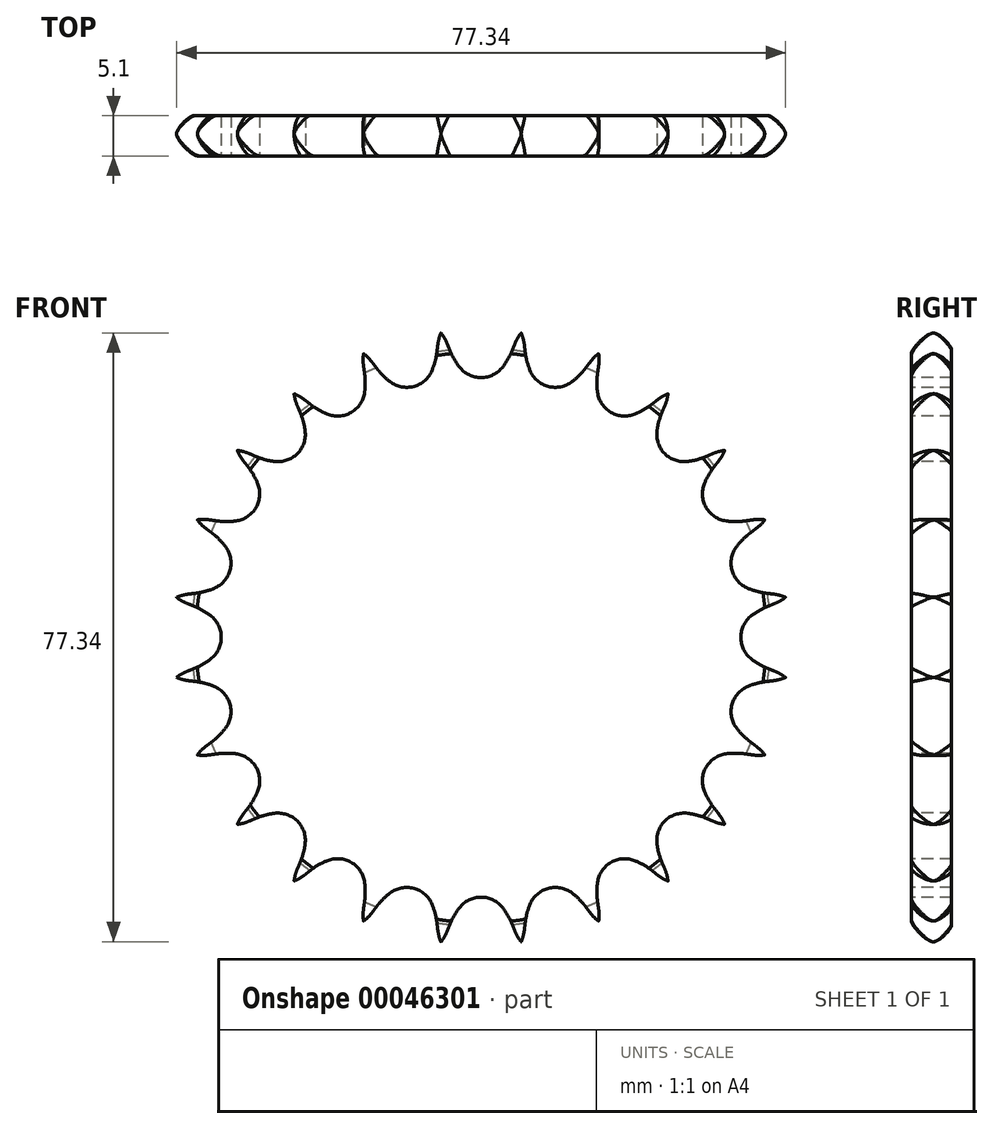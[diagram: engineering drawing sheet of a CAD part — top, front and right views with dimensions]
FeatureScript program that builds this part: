
annotation { "Feature Type Name" : "Feature", "Feature Type Description" : "" }
export const myFeature = defineFeature(function(context is Context, id is Id, definition is map)
    precondition{}
    {
        {
            var Q0;
            Q0=qCreatedBy(makeId("Right.planeOp"),FACE);
            var sketch = newSketch(context, id + "F0", { "sketchPlane" : qUnion([Q0])});
            skLineSegment(sketch, "E0", {"start": v(0, 0) * mm, "end": v(5.1, 0) * mm, "construction": true});
            skLineSegment(sketch, "E1", {"start": v(0, 39) * mm, "end": v(5.1, 39) * mm});
            skLineSegment(sketch, "E2", {"start": v(5.1, 39) * mm, "end": v(5.1, 30) * mm});
            skLineSegment(sketch, "E3", {"start": v(5.1, 30) * mm, "end": v(5.1, 30) * mm});
            skLineSegment(sketch, "E4", {"start": v(5.1, 30) * mm, "end": v(5.1, 0) * mm});
            skLineSegment(sketch, "E5", {"start": v(0, 0) * mm, "end": v(0, 39) * mm});
            skLineSegment(sketch, "E6.0.MirrorCS", {"start": v(0, -39) * mm, "end": v(5.1, -39) * mm});
            skLineSegment(sketch, "E6.1.MirrorCS", {"start": v(5.1, -39) * mm, "end": v(5.1, -30) * mm});
            skLineSegment(sketch, "E6.3.MirrorCS", {"start": v(5.1, -30) * mm, "end": v(5.1, 0) * mm});
            skLineSegment(sketch, "E6.4.MirrorCS", {"start": v(5.1, -30) * mm, "end": v(5.1, -30) * mm});
            skLineSegment(sketch, "E6.5.MirrorCS", {"start": v(0, 0) * mm, "end": v(0, -39) * mm});
            skLineSegment(sketch, "E7", {"start": v(0, 0) * mm, "end": v(5.1, 0) * mm});
            skLineSegment(sketch, "E8", {"start": v(5.1, 30) * mm, "end": v(0, 30) * mm, "construction": true});
            skLineSegment(sketch, "E9", {"start": v(5.1, -30) * mm, "end": v(0, -30) * mm, "construction": true});
            skSolve(sketch);
        }
        {
            var Q0;
            Q0=makeQuery(id+"F0.imprint","IMPRINT",FACE,{"disambiguationData":[TD([[makeQuery(id+"F0.imprint","IMPRINT",EDGE,{"derivedFrom":sQuery(id+"F0.wireOp",EDGE,"E1")}),-1.0]])]});
            var Q1;
            Q1=sQuery(id+"F0.wireOp",EDGE,"E0");
            revolve(context, id + "F1", {"entities" : qUnion([Q0]), "axis" : qUnion([Q1]), "revolveType" : RevolveType.FULL});
        }
        {
            var Q0;
            Q0=makeQuery(id+"F1.opRevolve","SWEPT_EDGE",EDGE,{"disambiguationData":[OSD([sQuery(id+"F0.wireOp",EDGE,"E1"),sQuery(id+"F0.wireOp",EDGE,"E5")])]});
            fillet(context, id + "F2", {"entities" : qUnion([Q0]), "radius" : 2.75 * mm, "tangentPropagation" : true, "rho" : 0.2, "crossSection" : FilletCrossSection.CONIC, "allowEdgeOverflow" : false});
        }
        {
            var Q0;
            Q0=makeQuery(id+"F1.opRevolve","SWEPT_EDGE",EDGE,{"disambiguationData":[OSD([sQuery(id+"F0.wireOp",EDGE,"E1"),sQuery(id+"F0.wireOp",EDGE,"E2")])]});
            fillet(context, id + "F3", {"entities" : qUnion([Q0]), "radius" : 2.25 * mm, "tangentPropagation" : true, "rho" : 0.2, "crossSection" : FilletCrossSection.CONIC, "allowEdgeOverflow" : false});
        }
        {
            var Q0;
            Q0=qCreatedBy(makeId("Front.planeOp"),FACE);
            var sketch = newSketch(context, id + "F4", { "sketchPlane" : qUnion([Q0])});
            skPoint(sketch, "E10.0", {"position": v(0, 0) * mm});
            skLineSegment(sketch, "E11", {"start": v(0, 0) * mm, "end": v(0, 36.49) * mm, "construction": true});
            skLineSegment(sketch, "E12", {"start": v(0, 36.49) * mm, "end": v(75.89, 36.49) * mm, "construction": true});
            skLineSegment(sketch, "E13", {"start": v(0, 0) * mm, "end": v(-5.1, 38.69) * mm, "construction": true});
            skArc(sketch, "E14", {"start": v(-2.76, 34.37) * mm, "mid": v(12.15, 44.27) * mm, "end": v(-3.97, 36.5) * mm, "construction": true});
            skLineSegment(sketch, "E15", {"start": v(0, 0) * mm, "end": v(15.68, 0) * mm, "construction": true});
            skArc(sketch, "E16", {"start": v(-5.1, 38.69) * mm, "mid": v(-14.39, 32.43) * mm, "end": v(-4.3, 37.32) * mm, "construction": true});
            skLineSegment(sketch, "E17", {"start": v(0.64, 24.97) * mm, "end": v(-4.3, 37.32) * mm, "construction": true});
            skArc(sketch, "E18", {"start": v(2.76, 34.37) * mm, "mid": v(0, 39.97) * mm, "end": v(-2.76, 34.37) * mm, "construction": true});
            skArc(sketch, "E19.0.MirrorCS", {"start": v(3.97, 36.5) * mm, "mid": v(3.44, 35.39) * mm, "end": v(2.76, 34.37) * mm});
            skLineSegment(sketch, "E20.0.MirrorCS", {"start": v(3.97, 36.5) * mm, "end": v(4.3, 37.32) * mm});
            skArc(sketch, "E21", {"start": v(-2.76, 34.37) * mm, "mid": v(0, 33) * mm, "end": v(2.76, 34.37) * mm});
            skLineSegment(sketch, "E22", {"start": v(0, 36.49) * mm, "end": v(4.35, 39.83) * mm, "construction": true});
            skLineSegment(sketch, "E23", {"start": v(4.35, 39.83) * mm, "end": v(-3.97, 36.5) * mm, "construction": true});
            skLineSegment(sketch, "E24", {"start": v(-3.97, 36.5) * mm, "end": v(-4.3, 37.32) * mm});
            skArc(sketch, "E25", {"start": v(-4.3, 37.32) * mm, "mid": v(-4.65, 38.03) * mm, "end": v(-5.1, 38.69) * mm});
            skArc(sketch, "E26", {"start": v(-3.97, 36.5) * mm, "mid": v(-3.44, 35.39) * mm, "end": v(-2.76, 34.37) * mm});
            skArc(sketch, "E27.0.MirrorCS", {"start": v(4.3, 37.32) * mm, "mid": v(4.65, 38.03) * mm, "end": v(5.1, 38.69) * mm});
            skCircle(sketch, "E28", {"center": v(0, 0) * mm, "radius": 36.49 * mm, "construction": true});
            skArc(sketch, "E29.1.0", {"start": v(-13.82, 34.93) * mm, "mid": v(-14.34, 35.53) * mm, "end": v(-14.93, 36.05) * mm});
            skLineSegment(sketch, "E29.1.1", {"start": v(-13.28, 34.22) * mm, "end": v(-13.82, 34.93) * mm});
            skArc(sketch, "E29.1.2", {"start": v(-13.28, 34.22) * mm, "mid": v(-12.48, 33.29) * mm, "end": v(-11.56, 32.48) * mm});
            skArc(sketch, "E29.1.3", {"start": v(-11.56, 32.48) * mm, "mid": v(-8.54, 31.88) * mm, "end": v(-6.22, 33.9) * mm});
            skArc(sketch, "E29.1.4", {"start": v(-5.6, 36.28) * mm, "mid": v(-5.83, 35.07) * mm, "end": v(-6.22, 33.9) * mm});
            skLineSegment(sketch, "E29.1.5", {"start": v(-5.6, 36.28) * mm, "end": v(-5.5, 37.16) * mm});
            skArc(sketch, "E29.1.6", {"start": v(-5.5, 37.16) * mm, "mid": v(-5.35, 37.94) * mm, "end": v(-5.1, 38.69) * mm});
            skArc(sketch, "E29.2.0", {"start": v(-22.4, 30.17) * mm, "mid": v(-23.05, 30.61) * mm, "end": v(-23.76, 30.96) * mm});
            skLineSegment(sketch, "E29.2.1", {"start": v(-21.69, 29.61) * mm, "end": v(-22.4, 30.17) * mm});
            skArc(sketch, "E29.2.2", {"start": v(-21.69, 29.61) * mm, "mid": v(-20.67, 28.92) * mm, "end": v(-19.58, 28.38) * mm});
            skArc(sketch, "E29.2.3", {"start": v(-19.58, 28.38) * mm, "mid": v(-16.5, 28.58) * mm, "end": v(-14.79, 31.14) * mm});
            skArc(sketch, "E29.2.4", {"start": v(-14.8, 33.59) * mm, "mid": v(-14.71, 32.37) * mm, "end": v(-14.79, 31.14) * mm});
            skLineSegment(sketch, "E29.2.5", {"start": v(-14.8, 33.59) * mm, "end": v(-14.93, 34.47) * mm});
            skArc(sketch, "E29.2.6", {"start": v(-14.93, 34.47) * mm, "mid": v(-14.99, 35.26) * mm, "end": v(-14.93, 36.05) * mm});
            skArc(sketch, "E29.3.0", {"start": v(-29.44, 23.34) * mm, "mid": v(-30.18, 23.6) * mm, "end": v(-30.96, 23.76) * mm});
            skLineSegment(sketch, "E29.3.1", {"start": v(-28.61, 23) * mm, "end": v(-29.44, 23.34) * mm});
            skArc(sketch, "E29.3.2", {"start": v(-28.61, 23) * mm, "mid": v(-27.46, 22.59) * mm, "end": v(-26.25, 22.35) * mm});
            skArc(sketch, "E29.3.3", {"start": v(-26.25, 22.35) * mm, "mid": v(-23.34, 23.34) * mm, "end": v(-22.35, 26.25) * mm});
            skArc(sketch, "E29.3.4", {"start": v(-23, 28.61) * mm, "mid": v(-22.59, 27.46) * mm, "end": v(-22.35, 26.25) * mm});
            skLineSegment(sketch, "E29.3.5", {"start": v(-23, 28.61) * mm, "end": v(-23.34, 29.44) * mm});
            skArc(sketch, "E29.3.6", {"start": v(-23.34, 29.44) * mm, "mid": v(-23.6, 30.18) * mm, "end": v(-23.76, 30.96) * mm});
            skArc(sketch, "E29.4.0", {"start": v(-34.47, 14.93) * mm, "mid": v(-35.26, 14.99) * mm, "end": v(-36.05, 14.93) * mm});
            skLineSegment(sketch, "E29.4.1", {"start": v(-33.59, 14.8) * mm, "end": v(-34.47, 14.93) * mm});
            skArc(sketch, "E29.4.2", {"start": v(-33.59, 14.8) * mm, "mid": v(-32.37, 14.71) * mm, "end": v(-31.14, 14.79) * mm});
            skArc(sketch, "E29.4.3", {"start": v(-31.14, 14.79) * mm, "mid": v(-28.58, 16.5) * mm, "end": v(-28.38, 19.58) * mm});
            skArc(sketch, "E29.4.4", {"start": v(-29.61, 21.69) * mm, "mid": v(-28.92, 20.67) * mm, "end": v(-28.38, 19.58) * mm});
            skLineSegment(sketch, "E29.4.5", {"start": v(-29.61, 21.69) * mm, "end": v(-30.17, 22.4) * mm});
            skArc(sketch, "E29.4.6", {"start": v(-30.17, 22.4) * mm, "mid": v(-30.61, 23.05) * mm, "end": v(-30.96, 23.76) * mm});
            skArc(sketch, "E29.5.0", {"start": v(-37.16, 5.5) * mm, "mid": v(-37.94, 5.35) * mm, "end": v(-38.69, 5.1) * mm});
            skLineSegment(sketch, "E29.5.1", {"start": v(-36.28, 5.6) * mm, "end": v(-37.16, 5.5) * mm});
            skArc(sketch, "E29.5.2", {"start": v(-36.28, 5.6) * mm, "mid": v(-35.07, 5.83) * mm, "end": v(-33.9, 6.22) * mm});
            skArc(sketch, "E29.5.3", {"start": v(-33.9, 6.22) * mm, "mid": v(-31.88, 8.54) * mm, "end": v(-32.48, 11.56) * mm});
            skArc(sketch, "E29.5.4", {"start": v(-34.22, 13.28) * mm, "mid": v(-33.29, 12.48) * mm, "end": v(-32.48, 11.56) * mm});
            skLineSegment(sketch, "E29.5.5", {"start": v(-34.22, 13.28) * mm, "end": v(-34.93, 13.82) * mm});
            skArc(sketch, "E29.5.6", {"start": v(-34.93, 13.82) * mm, "mid": v(-35.53, 14.34) * mm, "end": v(-36.05, 14.93) * mm});
            skArc(sketch, "E29.6.0", {"start": v(-37.32, -4.3) * mm, "mid": v(-38.03, -4.65) * mm, "end": v(-38.69, -5.1) * mm});
            skLineSegment(sketch, "E29.6.1", {"start": v(-36.5, -3.97) * mm, "end": v(-37.32, -4.3) * mm});
            skArc(sketch, "E29.6.2", {"start": v(-36.5, -3.97) * mm, "mid": v(-35.39, -3.44) * mm, "end": v(-34.37, -2.76) * mm});
            skArc(sketch, "E29.6.3", {"start": v(-34.37, -2.76) * mm, "mid": v(-33, 0) * mm, "end": v(-34.37, 2.76) * mm});
            skArc(sketch, "E29.6.4", {"start": v(-36.5, 3.97) * mm, "mid": v(-35.39, 3.44) * mm, "end": v(-34.37, 2.76) * mm});
            skLineSegment(sketch, "E29.6.5", {"start": v(-36.5, 3.97) * mm, "end": v(-37.32, 4.3) * mm});
            skArc(sketch, "E29.6.6", {"start": v(-37.32, 4.3) * mm, "mid": v(-38.03, 4.65) * mm, "end": v(-38.69, 5.1) * mm});
            skArc(sketch, "E29.7.0", {"start": v(-34.93, -13.82) * mm, "mid": v(-35.53, -14.34) * mm, "end": v(-36.05, -14.93) * mm});
            skLineSegment(sketch, "E29.7.1", {"start": v(-34.22, -13.28) * mm, "end": v(-34.93, -13.82) * mm});
            skArc(sketch, "E29.7.2", {"start": v(-34.22, -13.28) * mm, "mid": v(-33.29, -12.48) * mm, "end": v(-32.48, -11.56) * mm});
            skArc(sketch, "E29.7.3", {"start": v(-32.48, -11.56) * mm, "mid": v(-31.88, -8.54) * mm, "end": v(-33.9, -6.22) * mm});
            skArc(sketch, "E29.7.4", {"start": v(-36.28, -5.6) * mm, "mid": v(-35.07, -5.83) * mm, "end": v(-33.9, -6.22) * mm});
            skLineSegment(sketch, "E29.7.5", {"start": v(-36.28, -5.6) * mm, "end": v(-37.16, -5.5) * mm});
            skArc(sketch, "E29.7.6", {"start": v(-37.16, -5.5) * mm, "mid": v(-37.94, -5.35) * mm, "end": v(-38.69, -5.1) * mm});
            skArc(sketch, "E29.8.0", {"start": v(-30.17, -22.4) * mm, "mid": v(-30.61, -23.05) * mm, "end": v(-30.96, -23.76) * mm});
            skLineSegment(sketch, "E29.8.1", {"start": v(-29.61, -21.69) * mm, "end": v(-30.17, -22.4) * mm});
            skArc(sketch, "E29.8.2", {"start": v(-29.61, -21.69) * mm, "mid": v(-28.92, -20.67) * mm, "end": v(-28.38, -19.58) * mm});
            skArc(sketch, "E29.8.3", {"start": v(-28.38, -19.58) * mm, "mid": v(-28.58, -16.5) * mm, "end": v(-31.14, -14.79) * mm});
            skArc(sketch, "E29.8.4", {"start": v(-33.59, -14.8) * mm, "mid": v(-32.37, -14.71) * mm, "end": v(-31.14, -14.79) * mm});
            skLineSegment(sketch, "E29.8.5", {"start": v(-33.59, -14.8) * mm, "end": v(-34.47, -14.93) * mm});
            skArc(sketch, "E29.8.6", {"start": v(-34.47, -14.93) * mm, "mid": v(-35.26, -14.99) * mm, "end": v(-36.05, -14.93) * mm});
            skArc(sketch, "E29.9.0", {"start": v(-23.34, -29.44) * mm, "mid": v(-23.6, -30.18) * mm, "end": v(-23.76, -30.96) * mm});
            skLineSegment(sketch, "E29.9.1", {"start": v(-23, -28.61) * mm, "end": v(-23.34, -29.44) * mm});
            skArc(sketch, "E29.9.2", {"start": v(-23, -28.61) * mm, "mid": v(-22.59, -27.46) * mm, "end": v(-22.35, -26.25) * mm});
            skArc(sketch, "E29.9.3", {"start": v(-22.35, -26.25) * mm, "mid": v(-23.34, -23.34) * mm, "end": v(-26.25, -22.35) * mm});
            skArc(sketch, "E29.9.4", {"start": v(-28.61, -23) * mm, "mid": v(-27.46, -22.59) * mm, "end": v(-26.25, -22.35) * mm});
            skLineSegment(sketch, "E29.9.5", {"start": v(-28.61, -23) * mm, "end": v(-29.44, -23.34) * mm});
            skArc(sketch, "E29.9.6", {"start": v(-29.44, -23.34) * mm, "mid": v(-30.18, -23.6) * mm, "end": v(-30.96, -23.76) * mm});
            skArc(sketch, "E29.10.0", {"start": v(-14.93, -34.47) * mm, "mid": v(-14.99, -35.26) * mm, "end": v(-14.93, -36.05) * mm});
            skLineSegment(sketch, "E29.10.1", {"start": v(-14.8, -33.59) * mm, "end": v(-14.93, -34.47) * mm});
            skArc(sketch, "E29.10.2", {"start": v(-14.8, -33.59) * mm, "mid": v(-14.71, -32.37) * mm, "end": v(-14.79, -31.14) * mm});
            skArc(sketch, "E29.10.3", {"start": v(-14.79, -31.14) * mm, "mid": v(-16.5, -28.58) * mm, "end": v(-19.58, -28.38) * mm});
            skArc(sketch, "E29.10.4", {"start": v(-21.69, -29.61) * mm, "mid": v(-20.67, -28.92) * mm, "end": v(-19.58, -28.38) * mm});
            skLineSegment(sketch, "E29.10.5", {"start": v(-21.69, -29.61) * mm, "end": v(-22.4, -30.17) * mm});
            skArc(sketch, "E29.10.6", {"start": v(-22.4, -30.17) * mm, "mid": v(-23.05, -30.61) * mm, "end": v(-23.76, -30.96) * mm});
            skArc(sketch, "E29.11.0", {"start": v(-5.5, -37.16) * mm, "mid": v(-5.35, -37.94) * mm, "end": v(-5.1, -38.69) * mm});
            skLineSegment(sketch, "E29.11.1", {"start": v(-5.6, -36.28) * mm, "end": v(-5.5, -37.16) * mm});
            skArc(sketch, "E29.11.2", {"start": v(-5.6, -36.28) * mm, "mid": v(-5.83, -35.07) * mm, "end": v(-6.22, -33.9) * mm});
            skArc(sketch, "E29.11.3", {"start": v(-6.22, -33.9) * mm, "mid": v(-8.54, -31.88) * mm, "end": v(-11.56, -32.48) * mm});
            skArc(sketch, "E29.11.4", {"start": v(-13.28, -34.22) * mm, "mid": v(-12.48, -33.29) * mm, "end": v(-11.56, -32.48) * mm});
            skLineSegment(sketch, "E29.11.5", {"start": v(-13.28, -34.22) * mm, "end": v(-13.82, -34.93) * mm});
            skArc(sketch, "E29.11.6", {"start": v(-13.82, -34.93) * mm, "mid": v(-14.34, -35.53) * mm, "end": v(-14.93, -36.05) * mm});
            skArc(sketch, "E29.12.0", {"start": v(4.3, -37.32) * mm, "mid": v(4.65, -38.03) * mm, "end": v(5.1, -38.69) * mm});
            skLineSegment(sketch, "E29.12.1", {"start": v(3.97, -36.5) * mm, "end": v(4.3, -37.32) * mm});
            skArc(sketch, "E29.12.2", {"start": v(3.97, -36.5) * mm, "mid": v(3.44, -35.39) * mm, "end": v(2.76, -34.37) * mm});
            skArc(sketch, "E29.12.3", {"start": v(2.76, -34.37) * mm, "mid": v(0, -33) * mm, "end": v(-2.76, -34.37) * mm});
            skArc(sketch, "E29.12.4", {"start": v(-3.97, -36.5) * mm, "mid": v(-3.44, -35.39) * mm, "end": v(-2.76, -34.37) * mm});
            skLineSegment(sketch, "E29.12.5", {"start": v(-3.97, -36.5) * mm, "end": v(-4.3, -37.32) * mm});
            skArc(sketch, "E29.12.6", {"start": v(-4.3, -37.32) * mm, "mid": v(-4.65, -38.03) * mm, "end": v(-5.1, -38.69) * mm});
            skArc(sketch, "E29.13.0", {"start": v(13.82, -34.93) * mm, "mid": v(14.34, -35.53) * mm, "end": v(14.93, -36.05) * mm});
            skLineSegment(sketch, "E29.13.1", {"start": v(13.28, -34.22) * mm, "end": v(13.82, -34.93) * mm});
            skArc(sketch, "E29.13.2", {"start": v(13.28, -34.22) * mm, "mid": v(12.48, -33.29) * mm, "end": v(11.56, -32.48) * mm});
            skArc(sketch, "E29.13.3", {"start": v(11.56, -32.48) * mm, "mid": v(8.54, -31.88) * mm, "end": v(6.22, -33.9) * mm});
            skArc(sketch, "E29.13.4", {"start": v(5.6, -36.28) * mm, "mid": v(5.83, -35.07) * mm, "end": v(6.22, -33.9) * mm});
            skLineSegment(sketch, "E29.13.5", {"start": v(5.6, -36.28) * mm, "end": v(5.5, -37.16) * mm});
            skArc(sketch, "E29.13.6", {"start": v(5.5, -37.16) * mm, "mid": v(5.35, -37.94) * mm, "end": v(5.1, -38.69) * mm});
            skArc(sketch, "E29.14.0", {"start": v(22.4, -30.17) * mm, "mid": v(23.05, -30.61) * mm, "end": v(23.76, -30.96) * mm});
            skLineSegment(sketch, "E29.14.1", {"start": v(21.69, -29.61) * mm, "end": v(22.4, -30.17) * mm});
            skArc(sketch, "E29.14.2", {"start": v(21.69, -29.61) * mm, "mid": v(20.67, -28.92) * mm, "end": v(19.58, -28.38) * mm});
            skArc(sketch, "E29.14.3", {"start": v(19.58, -28.38) * mm, "mid": v(16.5, -28.58) * mm, "end": v(14.79, -31.14) * mm});
            skArc(sketch, "E29.14.4", {"start": v(14.8, -33.59) * mm, "mid": v(14.71, -32.37) * mm, "end": v(14.79, -31.14) * mm});
            skLineSegment(sketch, "E29.14.5", {"start": v(14.8, -33.59) * mm, "end": v(14.93, -34.47) * mm});
            skArc(sketch, "E29.14.6", {"start": v(14.93, -34.47) * mm, "mid": v(14.99, -35.26) * mm, "end": v(14.93, -36.05) * mm});
            skArc(sketch, "E29.15.0", {"start": v(29.44, -23.34) * mm, "mid": v(30.18, -23.6) * mm, "end": v(30.96, -23.76) * mm});
            skLineSegment(sketch, "E29.15.1", {"start": v(28.61, -23) * mm, "end": v(29.44, -23.34) * mm});
            skArc(sketch, "E29.15.2", {"start": v(28.61, -23) * mm, "mid": v(27.46, -22.59) * mm, "end": v(26.25, -22.35) * mm});
            skArc(sketch, "E29.15.3", {"start": v(26.25, -22.35) * mm, "mid": v(23.34, -23.34) * mm, "end": v(22.35, -26.25) * mm});
            skArc(sketch, "E29.15.4", {"start": v(23, -28.61) * mm, "mid": v(22.59, -27.46) * mm, "end": v(22.35, -26.25) * mm});
            skLineSegment(sketch, "E29.15.5", {"start": v(23, -28.61) * mm, "end": v(23.34, -29.44) * mm});
            skArc(sketch, "E29.15.6", {"start": v(23.34, -29.44) * mm, "mid": v(23.6, -30.18) * mm, "end": v(23.76, -30.96) * mm});
            skArc(sketch, "E29.16.0", {"start": v(34.47, -14.93) * mm, "mid": v(35.26, -14.99) * mm, "end": v(36.05, -14.93) * mm});
            skLineSegment(sketch, "E29.16.1", {"start": v(33.59, -14.8) * mm, "end": v(34.47, -14.93) * mm});
            skArc(sketch, "E29.16.2", {"start": v(33.59, -14.8) * mm, "mid": v(32.37, -14.71) * mm, "end": v(31.14, -14.79) * mm});
            skArc(sketch, "E29.16.3", {"start": v(31.14, -14.79) * mm, "mid": v(28.58, -16.5) * mm, "end": v(28.38, -19.58) * mm});
            skArc(sketch, "E29.16.4", {"start": v(29.61, -21.69) * mm, "mid": v(28.92, -20.67) * mm, "end": v(28.38, -19.58) * mm});
            skLineSegment(sketch, "E29.16.5", {"start": v(29.61, -21.69) * mm, "end": v(30.17, -22.4) * mm});
            skArc(sketch, "E29.16.6", {"start": v(30.17, -22.4) * mm, "mid": v(30.61, -23.05) * mm, "end": v(30.96, -23.76) * mm});
            skArc(sketch, "E29.17.0", {"start": v(37.16, -5.5) * mm, "mid": v(37.94, -5.35) * mm, "end": v(38.69, -5.1) * mm});
            skLineSegment(sketch, "E29.17.1", {"start": v(36.28, -5.6) * mm, "end": v(37.16, -5.5) * mm});
            skArc(sketch, "E29.17.2", {"start": v(36.28, -5.6) * mm, "mid": v(35.07, -5.83) * mm, "end": v(33.9, -6.22) * mm});
            skArc(sketch, "E29.17.3", {"start": v(33.9, -6.22) * mm, "mid": v(31.88, -8.54) * mm, "end": v(32.48, -11.56) * mm});
            skArc(sketch, "E29.17.4", {"start": v(34.22, -13.28) * mm, "mid": v(33.29, -12.48) * mm, "end": v(32.48, -11.56) * mm});
            skLineSegment(sketch, "E29.17.5", {"start": v(34.22, -13.28) * mm, "end": v(34.93, -13.82) * mm});
            skArc(sketch, "E29.17.6", {"start": v(34.93, -13.82) * mm, "mid": v(35.53, -14.34) * mm, "end": v(36.05, -14.93) * mm});
            skArc(sketch, "E29.18.0", {"start": v(37.32, 4.3) * mm, "mid": v(38.03, 4.65) * mm, "end": v(38.69, 5.1) * mm});
            skLineSegment(sketch, "E29.18.1", {"start": v(36.5, 3.97) * mm, "end": v(37.32, 4.3) * mm});
            skArc(sketch, "E29.18.2", {"start": v(36.5, 3.97) * mm, "mid": v(35.39, 3.44) * mm, "end": v(34.37, 2.76) * mm});
            skArc(sketch, "E29.18.3", {"start": v(34.37, 2.76) * mm, "mid": v(33, 0) * mm, "end": v(34.37, -2.76) * mm});
            skArc(sketch, "E29.18.4", {"start": v(36.5, -3.97) * mm, "mid": v(35.39, -3.44) * mm, "end": v(34.37, -2.76) * mm});
            skLineSegment(sketch, "E29.18.5", {"start": v(36.5, -3.97) * mm, "end": v(37.32, -4.3) * mm});
            skArc(sketch, "E29.18.6", {"start": v(37.32, -4.3) * mm, "mid": v(38.03, -4.65) * mm, "end": v(38.69, -5.1) * mm});
            skArc(sketch, "E29.19.0", {"start": v(34.93, 13.82) * mm, "mid": v(35.53, 14.34) * mm, "end": v(36.05, 14.93) * mm});
            skLineSegment(sketch, "E29.19.1", {"start": v(34.22, 13.28) * mm, "end": v(34.93, 13.82) * mm});
            skArc(sketch, "E29.19.2", {"start": v(34.22, 13.28) * mm, "mid": v(33.29, 12.48) * mm, "end": v(32.48, 11.56) * mm});
            skArc(sketch, "E29.19.3", {"start": v(32.48, 11.56) * mm, "mid": v(31.88, 8.54) * mm, "end": v(33.9, 6.22) * mm});
            skArc(sketch, "E29.19.4", {"start": v(36.28, 5.6) * mm, "mid": v(35.07, 5.83) * mm, "end": v(33.9, 6.22) * mm});
            skLineSegment(sketch, "E29.19.5", {"start": v(36.28, 5.6) * mm, "end": v(37.16, 5.5) * mm});
            skArc(sketch, "E29.19.6", {"start": v(37.16, 5.5) * mm, "mid": v(37.94, 5.35) * mm, "end": v(38.69, 5.1) * mm});
            skArc(sketch, "E29.20.0", {"start": v(30.17, 22.4) * mm, "mid": v(30.61, 23.05) * mm, "end": v(30.96, 23.76) * mm});
            skLineSegment(sketch, "E29.20.1", {"start": v(29.61, 21.69) * mm, "end": v(30.17, 22.4) * mm});
            skArc(sketch, "E29.20.2", {"start": v(29.61, 21.69) * mm, "mid": v(28.92, 20.67) * mm, "end": v(28.38, 19.58) * mm});
            skArc(sketch, "E29.20.3", {"start": v(28.38, 19.58) * mm, "mid": v(28.58, 16.5) * mm, "end": v(31.14, 14.79) * mm});
            skArc(sketch, "E29.20.4", {"start": v(33.59, 14.8) * mm, "mid": v(32.37, 14.71) * mm, "end": v(31.14, 14.79) * mm});
            skLineSegment(sketch, "E29.20.5", {"start": v(33.59, 14.8) * mm, "end": v(34.47, 14.93) * mm});
            skArc(sketch, "E29.20.6", {"start": v(34.47, 14.93) * mm, "mid": v(35.26, 14.99) * mm, "end": v(36.05, 14.93) * mm});
            skArc(sketch, "E29.21.0", {"start": v(23.34, 29.44) * mm, "mid": v(23.6, 30.18) * mm, "end": v(23.76, 30.96) * mm});
            skLineSegment(sketch, "E29.21.1", {"start": v(23, 28.61) * mm, "end": v(23.34, 29.44) * mm});
            skArc(sketch, "E29.21.2", {"start": v(23, 28.61) * mm, "mid": v(22.59, 27.46) * mm, "end": v(22.35, 26.25) * mm});
            skArc(sketch, "E29.21.3", {"start": v(22.35, 26.25) * mm, "mid": v(23.34, 23.34) * mm, "end": v(26.25, 22.35) * mm});
            skArc(sketch, "E29.21.4", {"start": v(28.61, 23) * mm, "mid": v(27.46, 22.59) * mm, "end": v(26.25, 22.35) * mm});
            skLineSegment(sketch, "E29.21.5", {"start": v(28.61, 23) * mm, "end": v(29.44, 23.34) * mm});
            skArc(sketch, "E29.21.6", {"start": v(29.44, 23.34) * mm, "mid": v(30.18, 23.6) * mm, "end": v(30.96, 23.76) * mm});
            skArc(sketch, "E29.22.0", {"start": v(14.93, 34.47) * mm, "mid": v(14.99, 35.26) * mm, "end": v(14.93, 36.05) * mm});
            skLineSegment(sketch, "E29.22.1", {"start": v(14.8, 33.59) * mm, "end": v(14.93, 34.47) * mm});
            skArc(sketch, "E29.22.2", {"start": v(14.8, 33.59) * mm, "mid": v(14.71, 32.37) * mm, "end": v(14.79, 31.14) * mm});
            skArc(sketch, "E29.22.3", {"start": v(14.79, 31.14) * mm, "mid": v(16.5, 28.58) * mm, "end": v(19.58, 28.38) * mm});
            skArc(sketch, "E29.22.4", {"start": v(21.69, 29.61) * mm, "mid": v(20.67, 28.92) * mm, "end": v(19.58, 28.38) * mm});
            skLineSegment(sketch, "E29.22.5", {"start": v(21.69, 29.61) * mm, "end": v(22.4, 30.17) * mm});
            skArc(sketch, "E29.22.6", {"start": v(22.4, 30.17) * mm, "mid": v(23.05, 30.61) * mm, "end": v(23.76, 30.96) * mm});
            skArc(sketch, "E29.23.0", {"start": v(5.5, 37.16) * mm, "mid": v(5.35, 37.94) * mm, "end": v(5.1, 38.69) * mm});
            skLineSegment(sketch, "E29.23.1", {"start": v(5.6, 36.28) * mm, "end": v(5.5, 37.16) * mm});
            skArc(sketch, "E29.23.2", {"start": v(5.6, 36.28) * mm, "mid": v(5.83, 35.07) * mm, "end": v(6.22, 33.9) * mm});
            skArc(sketch, "E29.23.3", {"start": v(6.22, 33.9) * mm, "mid": v(8.54, 31.88) * mm, "end": v(11.56, 32.48) * mm});
            skArc(sketch, "E29.23.4", {"start": v(13.28, 34.22) * mm, "mid": v(12.48, 33.29) * mm, "end": v(11.56, 32.48) * mm});
            skLineSegment(sketch, "E29.23.5", {"start": v(13.28, 34.22) * mm, "end": v(13.82, 34.93) * mm});
            skArc(sketch, "E29.23.6", {"start": v(13.82, 34.93) * mm, "mid": v(14.34, 35.53) * mm, "end": v(14.93, 36.05) * mm});
            skSolve(sketch);
        }
        {
            var Q0;
            Q0 = qSketchRegion(id + "F4", true);
            extrude(context, id + "F5", {"entities" : qUnion([Q0]), "operationType" : NewBodyOperationType.INTERSECT, "endBound" : BoundingType.THROUGH_ALL, "oppositeDirection" : true, "depth" : 25.4 * mm});
        }
    });
